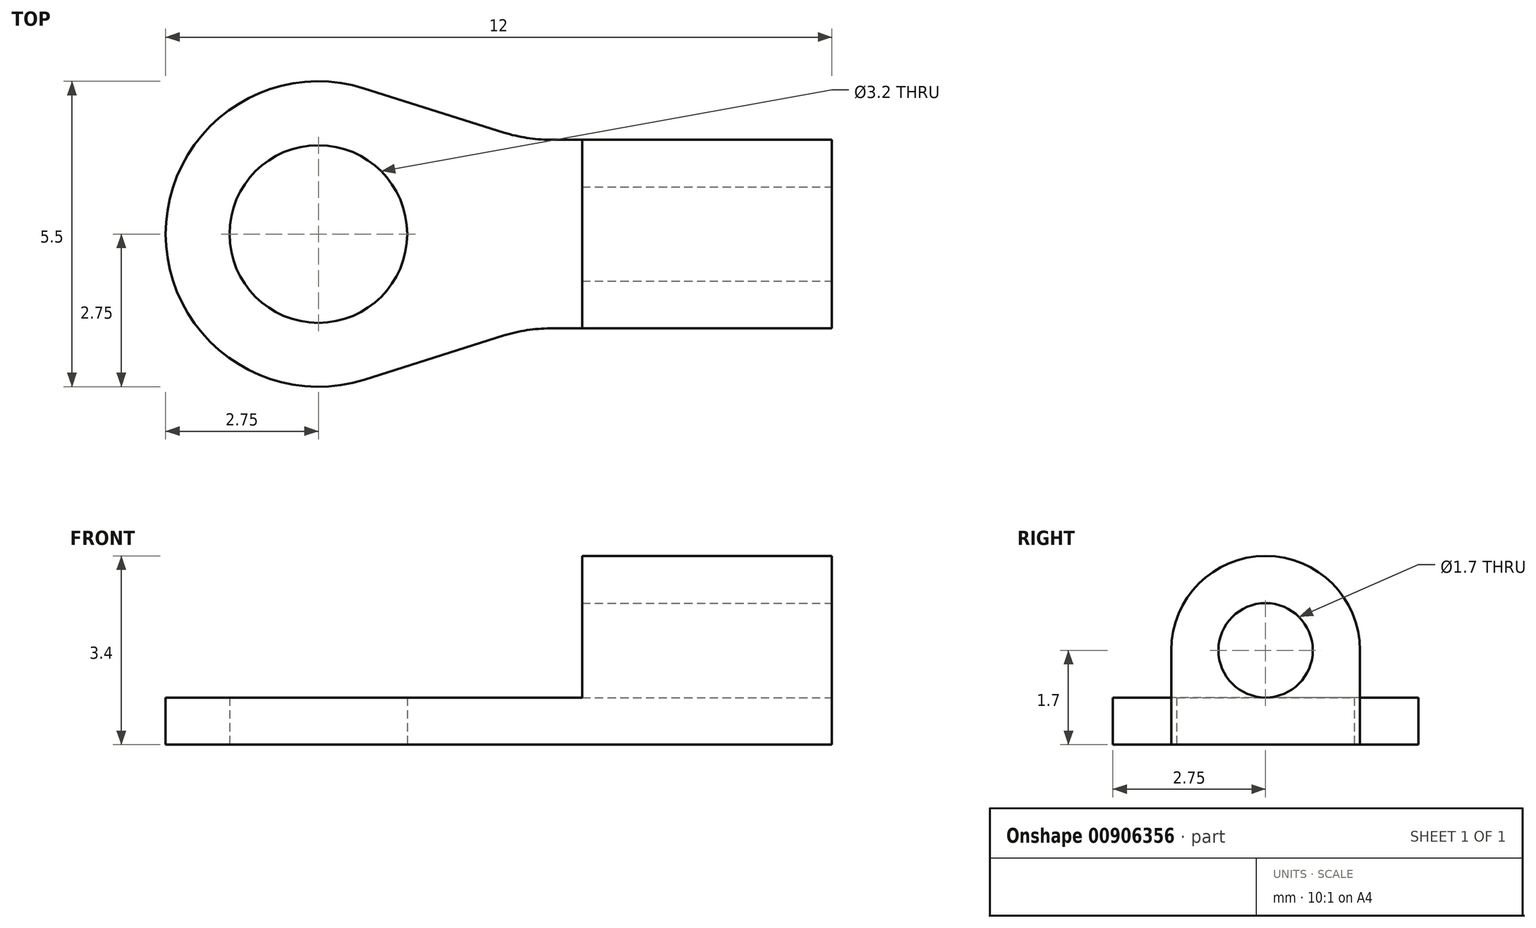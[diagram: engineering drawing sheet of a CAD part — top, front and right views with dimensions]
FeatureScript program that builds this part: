
annotation { "Feature Type Name" : "Feature", "Feature Type Description" : "" }
export const myFeature = defineFeature(function(context is Context, id is Id, definition is map)
    precondition{}
    {
        {
            var Q0;
            Q0=qCreatedBy(makeId("Top.planeOp"),FACE);
            var sketch = newSketch(context, id + "F0", { "sketchPlane" : qUnion([Q0])});
            skLineSegment(sketch, "E0.left", {"start": v(0, 2.75) * mm, "end": v(0, 2.75) * mm});
            skLineSegment(sketch, "E0.right", {"start": v(12, 1.05) * mm, "end": v(12, 4.45) * mm});
            skPoint(sketch, "E1.visualSharp", {"position": v(0, 5.5) * mm});
            skArc(sketch, "E1.filletArc", {"start": v(2.75, 5.5) * mm, "mid": v(0.8, 4.7) * mm, "end": v(0, 2.75) * mm});
            skPoint(sketch, "E2.visualSharp", {"position": v(0, 0) * mm});
            skArc(sketch, "E2.filletArc", {"start": v(0, 2.75) * mm, "mid": v(0.8, 0.8) * mm, "end": v(2.75, 0) * mm});
            skLineSegment(sketch, "E3.0", {"start": v(6.5, 1.02) * mm, "end": v(6.5, 1.05) * mm});
            skCircle(sketch, "E4", {"center": v(2.75, 2.75) * mm, "radius": 1.6 * mm});
            skLineSegment(sketch, "E5.0", {"start": v(12, 4.45) * mm, "end": v(6.92, 4.45) * mm});
            skLineSegment(sketch, "E6.MirrorCS", {"start": v(12, 1.05) * mm, "end": v(6.92, 1.05) * mm});
            skArc(sketch, "E7", {"start": v(3.58, 5.37) * mm, "mid": v(0, 2.75) * mm, "end": v(3.58, 0.13) * mm});
            skLineSegment(sketch, "E8", {"start": v(6.1, 4.58) * mm, "end": v(3.58, 5.37) * mm});
            skLineSegment(sketch, "E9", {"start": v(6.1, 0.92) * mm, "end": v(3.58, 0.13) * mm});
            skPoint(sketch, "E10.visualSharp", {"position": v(6.5, 4.45) * mm});
            skArc(sketch, "E10.filletArc", {"start": v(6.1, 4.58) * mm, "mid": v(6.5, 4.48) * mm, "end": v(6.92, 4.45) * mm});
            skPoint(sketch, "E11.visualSharp", {"position": v(6.5, 1.05) * mm});
            skArc(sketch, "E11.filletArc", {"start": v(6.92, 1.05) * mm, "mid": v(6.5, 1.02) * mm, "end": v(6.1, 0.92) * mm});
            skPoint(sketch, "E12.orphan", {"position": v(12, 2.75) * mm});
            skPoint(sketch, "E13.end.orphan", {"position": v(6.5, 2.75) * mm});
            skLineSegment(sketch, "E14.trimOffspring", {"start": v(6.5, 4.45) * mm, "end": v(6.5, 4.48) * mm});
            skPoint(sketch, "E15.orphan", {"position": v(6.5, 5.5) * mm});
            skPoint(sketch, "E16.orphan", {"position": v(12, 5.5) * mm});
            skPoint(sketch, "E17.orphan", {"position": v(12, 0) * mm});
            skPoint(sketch, "E0.bottom.end.orphan", {"position": v(6.5, 0) * mm});
            skSolve(sketch);
        }
        {
            var Q0;
            Q0=makeQuery(id+"F0.imprint","IMPRINT",FACE,{"disambiguationData":[TD([[makeQuery(id+"F0.imprint","IMPRINT",EDGE,{"derivedFrom":sQuery(id+"F0.wireOp",EDGE,"E0.right")}),1.0]])]});
            extrude(context, id + "F1", {"entities" : qUnion([Q0]), "depth" : 0.85 * mm, "offsetDistance" : 25 * mm});
        }
        {
            var Q0;
            Q0=makeQuery(id+"F1.opExtrude","CAP_FACE",FACE,{"disambiguationData":[OSD([sQuery(id+"F0.wireOp",EDGE,"E0.right"),sQuery(id+"F0.wireOp",EDGE,"E4"),sQuery(id+"F0.wireOp",EDGE,"E5.0"),sQuery(id+"F0.wireOp",EDGE,"E6.MirrorCS"),sQuery(id+"F0.wireOp",EDGE,"E7"),sQuery(id+"F0.wireOp",EDGE,"E8"),sQuery(id+"F0.wireOp",EDGE,"E9"),sQuery(id+"F0.wireOp",EDGE,"E10.filletArc"),sQuery(id+"F0.wireOp",EDGE,"E11.filletArc")])],"isStart":false});
            var sketch = newSketch(context, id + "F2", { "sketchPlane" : qUnion([Q0])});
            skLineSegment(sketch, "E18.bottom", {"start": v(12, 4.45) * mm, "end": v(7.5, 4.45) * mm});
            skLineSegment(sketch, "E18.top", {"start": v(12, 1.05) * mm, "end": v(7.5, 1.05) * mm});
            skLineSegment(sketch, "E18.left", {"start": v(12, 4.45) * mm, "end": v(12, 1.05) * mm});
            skLineSegment(sketch, "E18.right", {"start": v(7.5, 4.45) * mm, "end": v(7.5, 1.05) * mm});
            skSolve(sketch);
        }
        {
            var Q0;
            Q0 = qSketchRegion(id + "F2", true);
            extrude(context, id + "F3", {"entities" : qUnion([Q0]), "operationType" : NewBodyOperationType.ADD, "depth" : 2.55 * mm, "offsetDistance" : 25 * mm});
        }
        {
            var Q0;
            Q0=makeQuery(id+"F3.opExtrude","CAP_EDGE",EDGE,{"disambiguationData":[OSD([sQuery(id+"F2.wireOp",EDGE,"E18.bottom")])],"isStart":false});
            var Q1;
            Q1=makeQuery(id+"F3.opExtrude","CAP_EDGE",EDGE,{"disambiguationData":[OSD([sQuery(id+"F2.wireOp",EDGE,"E18.top")])],"isStart":false});
            fillet(context, id + "F4", {"entities" : qUnion([Q0, Q1]), "radius" : 1.7 * mm, "tangentPropagation" : true, "allowEdgeOverflow" : false});
        }
        {
            var Q0;
            Q0=makeQuery(id+"F3.boolean.opBoolean","MERGE",FACE,{"derivedFrom":[makeQuery(id+"F1.opExtrude","SWEPT_FACE",FACE,{"disambiguationData":[OSD([sQuery(id+"F0.wireOp",EDGE,"E0.right")])]}),makeQuery(id+"F3.opExtrude","SWEPT_FACE",FACE,{"disambiguationData":[OSD([sQuery(id+"F2.wireOp",EDGE,"E18.left")])]})]});
            var sketch = newSketch(context, id + "F5", { "sketchPlane" : qUnion([Q0])});
            skCircle(sketch, "E19", {"center": v(2.75, 1.7) * mm, "radius": 0.85 * mm});
            skSolve(sketch);
        }
        {
            var Q0;
            Q0=makeQuery(id+"F5.imprint","IMPRINT",FACE,{"disambiguationData":[TD([[makeQuery(id+"F5.imprint","IMPRINT",EDGE,{"derivedFrom":sQuery(id+"F5.wireOp",EDGE,"E19")}),1.0]])]});
            extrude(context, id + "F6", {"entities" : qUnion([Q0]), "operationType" : NewBodyOperationType.REMOVE, "oppositeDirection" : true, "depth" : 25 * mm, "offsetDistance" : 25 * mm});
        }
    });
